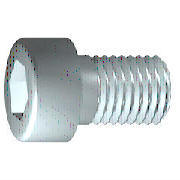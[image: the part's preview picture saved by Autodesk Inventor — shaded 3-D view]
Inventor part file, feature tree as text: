
AUTODESK INVENTOR PART (.ipt)
format: ipt  version: 2021 (Build 250183000, 183)  size: 193,024 bytes
history: native  units: mm (DEFAULTED — no unit token found)
features: sketch x2, extrude x1, plane x1, fillet x1
ambient origin geometry x7: Origin, YZ Plane, XY Plane, X Axis, Y Axis, Z Axis, Center Point
bodies: Solid1 (feature_tree), Body (feature_tree)
feature tree (5):
  extrude  "Slot"  Depth=2.0mm
  plane  "Work Plane1"
  fillet  "Fillet2"  Radius=2.0mm
  sketch  "Sketch1"  dims[d1=7.0mm d2=0.24548mm d3=2.0mm]
  sketch  "Sketch2"  dims[d4=1.0mm d5=60.0deg d6=2.0mm d7=2.0mm d8=1.732051mm d9=3.8mm d10=90.0deg d11=10.0mm d12=0.0mm d13=7.0mm d14=0.0mm d15=0.24538mm d16=0.24538mm d17=0.2mm d19=0.0mm d26=8.0mm d27=45.0deg d28=0.0mm d29=0.0mm d30=0.1mm]
